# Revit family: NBS_WallgateLtd_PrxmtySnsrCtrlUnits_WDC400
name_source: partatom
category: Mechanical Equipment
revit_build: Autodesk Revit 2014 (Build: 20130709_2115(x64)
units: mm (PartAtom-declared; Revit-internal decimal feet)

## types (1)
- WDC400
    AccessoryOptions = CISTFV Electronic cisterns, FVA Non-Potable Direct Flush Valves, DFKIT Potable Direct Flush Valves, WVC Flush Valve Cables, PBA Piezo Touch Buttons, PBA-IR Infra-Red Activation Sensors, WVPB Basin Water Valve Pack, WVPS Shower Water Valve Pack, CLS Key Lock Switches, LSC Light Switch Cables
    ApplicationOptions = Central or stand alone
    AssetType = Fixed
    BIMObjectName = NBS_WallgateLtd_ProximitySensorControlUnits_WDC400
    ControlType = Unset
    Description = Electronic Controller with the bbility to manage sanitary ware water flow, lighting and ring main to two rooms
    DurationUnit = year
    ElectricalDeviceNominalPower = 3000
    Features = Highly energy and water efficient, easily programmable - locally or networked
    HasProtectiveEarth = Yes
    IP_Code = IP53
    IfcExportAs = IfcControllerType
    IfcExportType = NOTDEFINED
    InsulationStandardClass = Class 1
    ManufacturerName = Wallgate Ltd
    ManufacturerURL = www.wallgate.com
    ModelNumber = WDC400
    Mounting = Wall mounted
    NBSCertification = www.nationalbimlibrary.com/cert/czjotfpu
    NBSDescription = Proximity sensor control units
    NBSReference = 45-35-70/422
    Name = ProximitySensorControlUnits_WDC400_WallgateLtd
    NominalCurrent = 0
    NominalFrequencyRange = 50.0 , 60.0
    NominalHeight = 460 mm
    NominalLength = 133 mm  [stored 0.436352 ft]
    NominalVoltage = 240.0 , 240.0
    NominalWidth = 280 mm
    NumberOfPoles = 2
    OutletNumber = 8
    PhaseAngle = 0.00°
    PhaseReference = Single phase
    ProductInformation = www.wallgate.com/products/washroom-controls/wdc-electronic-controller-range
    SensorControlMaterial = NBS_Concept
    SignalFactor = 0
    SignalOffset = 0
    SignalTime = 0
    Size = 460 x 280 x 133 mm
    ThirdPartyCertification = IEC60439-1, IEC61000, LVD 2006/95/EC & EMC 2004/108/EC
    Uniclass2 = 45-51-53/465
    UsageCurrent = 0
    Version = 1
    WarrantyDurationParts = 1
    WarrantyDurationUnit = year
    Weight = 8.0 kg

note: [stored X ft] marks values corroborated as IEEE doubles in the binary element streams (Revit-internal decimal feet)

## geometry (parser evidence)
native form markers: Sweep x1
no freeform markers — native parametric forms only
